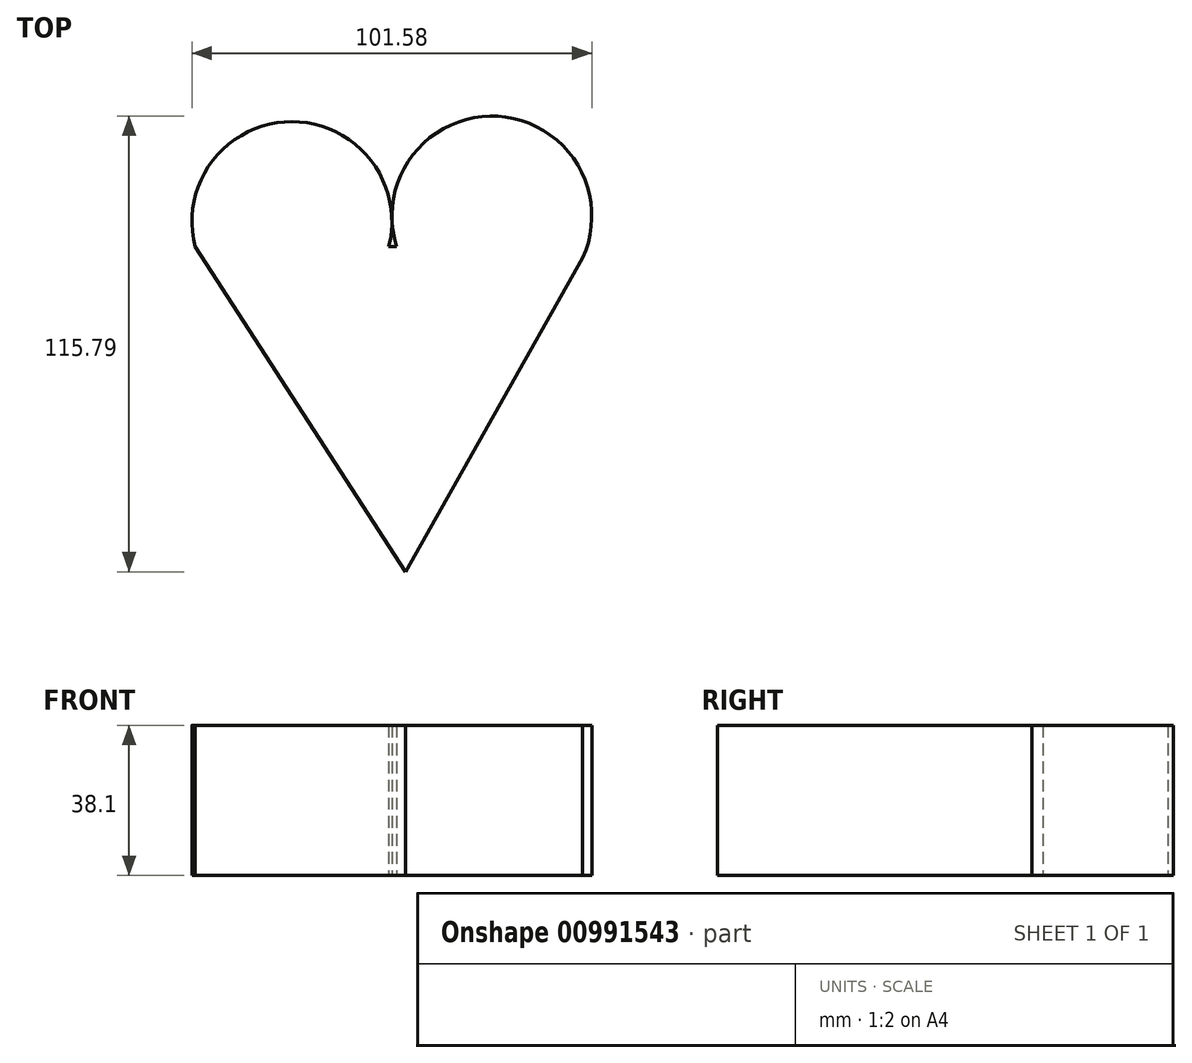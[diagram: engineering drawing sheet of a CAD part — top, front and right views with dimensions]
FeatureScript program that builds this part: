
annotation { "Feature Type Name" : "Feature", "Feature Type Description" : "" }
export const myFeature = defineFeature(function(context is Context, id is Id, definition is map)
    precondition{}
    {
        {
            var Q0;
            Q0=qCreatedBy(makeId("Top.planeOp"),FACE);
            var sketch = newSketch(context, id + "F0", { "sketchPlane" : qUnion([Q0])});
            skArc(sketch, "E0", {"start": v(-61.37, 37.69) * mm, "mid": v(-85.96, 69.43) * mm, "end": v(-110.56, 37.69) * mm});
            skArc(sketch, "E1", {"start": v(-12.1, 34.81) * mm, "mid": v(-33.64, 70.78) * mm, "end": v(-59.37, 37.69) * mm});
            skLineSegment(sketch, "E2.bottom", {"start": v(-61.37, 37.69) * mm, "end": v(-59.37, 37.69) * mm});
            skLineSegment(sketch, "E3", {"start": v(-110.56, 37.69) * mm, "end": v(-57.08, -44.96) * mm});
            skLineSegment(sketch, "E4", {"start": v(-12.1, 34.81) * mm, "end": v(-57.08, -44.96) * mm});
            skLineSegment(sketch, "E5.trimOffspring", {"start": v(-10.99, 37.69) * mm, "end": v(-10.48, 37.69) * mm});
            skSolve(sketch);
        }
        {
            var Q0;
            Q0=makeQuery(id+"F0.imprint","IMPRINT",FACE,{"disambiguationData":[TD([[makeQuery(id+"F0.imprint","IMPRINT",EDGE,{"derivedFrom":sQuery(id+"F0.wireOp",EDGE,"E0")}),1.0]])]});
            extrude(context, id + "F1", {"entities" : qUnion([Q0]), "depth" : 38.1 * mm, "offsetDistance" : 25.4 * mm});
        }
    });
